# Revit family: TP Lite Glass Panel
name_source: partatom
category: Curtain Panels
revit_build: Autodesk Revit Architecture 2012 (Build: 20110916_2132)
units: mm (PartAtom-declared; Revit-internal decimal feet)

## types (7) — shared parameters
Glass = Triplan Glass
Manufacturer = Triplan International A/S
URL = http://www.triplan.net
zero-valued in all types: Offset

## per-type parameters (varying)
| type | FireRating | SoundReduction | Thickness |
| TP Lite 1 |  | 36 RW db | 12 mm  [stored 0.0393701 ft] |
| TP Lite 2 |  | 36 RW db | 12 mm  [stored 0.0393701 ft] |
| TP Lite 3 |  | 38 RW db | 10.38 mm  [stored 0.0340551 ft] |
| TP Lite 4 |  | 39 RW db | 12.76 mm  [stored 0.0418635 ft] |
| TP Lite 5 |  | 42 RW db | 16.76 mm  [stored 0.0549869 ft] |
| TP Lite 6 | EI30 | 40 RW db | 23 mm  [stored 0.0754593 ft] |
| TP Lite 7 | EI60 | 42 RW db | 31 mm  [stored 0.101706 ft] |

note: [stored X ft] marks values corroborated as IEEE doubles in the binary element streams (Revit-internal decimal feet)

## geometry (parser evidence)
native form markers: Sweep x5
no freeform markers — native parametric forms only
